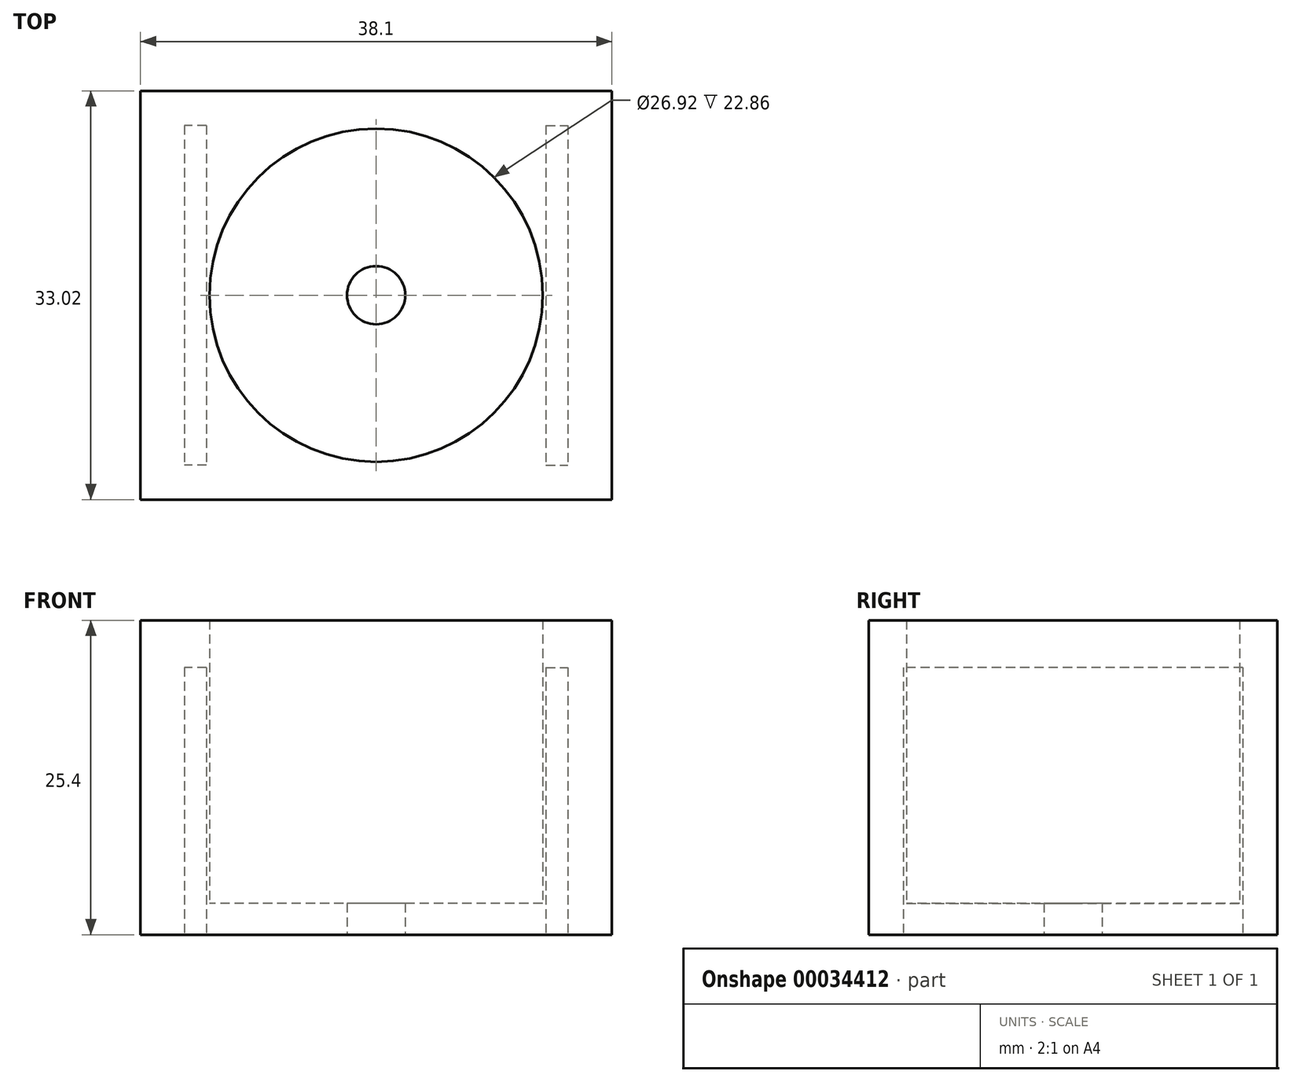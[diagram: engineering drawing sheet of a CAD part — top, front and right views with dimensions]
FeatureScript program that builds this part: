
annotation { "Feature Type Name" : "Feature", "Feature Type Description" : "" }
export const myFeature = defineFeature(function(context is Context, id is Id, definition is map)
    precondition{}
    {
        {
            var Q0;
            Q0=qCreatedBy(makeId("Top.planeOp"),FACE);
            var sketch = newSketch(context, id + "F0", { "sketchPlane" : qUnion([Q0])});
            skLineSegment(sketch, "E0.rect.bottom", {"start": v(19.05, 16.51) * mm, "end": v(-19.05, 16.51) * mm});
            skLineSegment(sketch, "E0.rect.top", {"start": v(19.05, -16.51) * mm, "end": v(-19.05, -16.51) * mm});
            skLineSegment(sketch, "E0.rect.left", {"start": v(19.05, 16.51) * mm, "end": v(19.05, -16.51) * mm});
            skLineSegment(sketch, "E0.rect.right", {"start": v(-19.05, 16.51) * mm, "end": v(-19.05, -16.51) * mm});
            skPoint(sketch, "E0.rect.middle", {"position": v(0, 0) * mm});
            skCircle(sketch, "E1", {"center": v(0, 0) * mm, "radius": 2.35 * mm});
            skSolve(sketch);
        }
        {
            var Q0;
            Q0=makeQuery(id+"F0.imprint","IMPRINT",FACE,{"disambiguationData":[TD([[makeQuery(id+"F0.imprint","IMPRINT",EDGE,{"derivedFrom":sQuery(id+"F0.wireOp",EDGE,"E0.rect.bottom")}),1.0]])]});
            extrude(context, id + "F1", {"entities" : qUnion([Q0]), "depth" : 2.54 * mm});
        }
        {
            var Q0;
            Q0=makeQuery(id+"F1.opExtrude","CAP_FACE",FACE,{"disambiguationData":[OSD([sQuery(id+"F0.wireOp",EDGE,"E0.rect.bottom"),sQuery(id+"F0.wireOp",EDGE,"E0.rect.top"),sQuery(id+"F0.wireOp",EDGE,"E0.rect.left"),sQuery(id+"F0.wireOp",EDGE,"E0.rect.right"),sQuery(id+"F0.wireOp",EDGE,"E1")])],"isStart":false});
            var sketch = newSketch(context, id + "F2", { "sketchPlane" : qUnion([Q0])});
            skCircle(sketch, "E2", {"center": v(0, 0) * mm, "radius": 13.46 * mm});
            skSolve(sketch);
        }
        {
            var Q0;
            Q0=makeQuery(id+"F2.imprint","IMPRINT",FACE,{"disambiguationData":[TD([[makeQuery(id+"F2.imprint","IMPRINT",EDGE,{"derivedFrom":sQuery(id+"F2.wireOp",EDGE,"E2")}),-1.0]])]});
            extrude(context, id + "F3", {"entities" : qUnion([Q0]), "operationType" : NewBodyOperationType.ADD, "depth" : 22.86 * mm});
        }
        {
            var Q0;
            Q0=makeQuery(id+"F1.opExtrude","CAP_FACE",FACE,{"disambiguationData":[OSD([sQuery(id+"F0.wireOp",EDGE,"E0.rect.bottom"),sQuery(id+"F0.wireOp",EDGE,"E0.rect.top"),sQuery(id+"F0.wireOp",EDGE,"E0.rect.left"),sQuery(id+"F0.wireOp",EDGE,"E0.rect.right"),sQuery(id+"F0.wireOp",EDGE,"E1")])],"isStart":true});
            var sketch = newSketch(context, id + "F4", { "sketchPlane" : qUnion([Q0])});
            skLineSegment(sketch, "E3", {"start": v(0, -16.51) * mm, "end": v(0, 16.51) * mm, "construction": true});
            skLineSegment(sketch, "E4", {"start": v(19.05, 0) * mm, "end": v(-19.05, 0) * mm, "construction": true});
            skLineSegment(sketch, "E5.rect.bottom", {"start": v(-13.72, -13.72) * mm, "end": v(-15.5, -13.72) * mm});
            skLineSegment(sketch, "E5.rect.top", {"start": v(-13.72, 13.72) * mm, "end": v(-15.5, 13.72) * mm});
            skLineSegment(sketch, "E5.rect.left", {"start": v(-13.72, -13.72) * mm, "end": v(-13.72, 13.72) * mm});
            skLineSegment(sketch, "E5.rect.right", {"start": v(-15.5, -13.72) * mm, "end": v(-15.5, 13.72) * mm});
            skPoint(sketch, "E5.rect.middle", {"position": v(-14.6, 0) * mm});
            skLineSegment(sketch, "E6.MirrorCS", {"start": v(13.72, -13.72) * mm, "end": v(13.72, 13.72) * mm});
            skLineSegment(sketch, "E7.MirrorCS", {"start": v(15.5, -13.72) * mm, "end": v(15.5, 13.72) * mm});
            skLineSegment(sketch, "E8.MirrorCS", {"start": v(13.72, -13.72) * mm, "end": v(15.5, -13.72) * mm});
            skLineSegment(sketch, "E9.MirrorCS", {"start": v(13.72, 13.72) * mm, "end": v(15.5, 13.72) * mm});
            skSolve(sketch);
        }
        {
            var Q0;
            Q0=makeQuery(id+"F4.imprint","IMPRINT",FACE,{"disambiguationData":[TD([[makeQuery(id+"F4.imprint","IMPRINT",EDGE,{"derivedFrom":sQuery(id+"F4.wireOp",EDGE,"E6.MirrorCS")}),-1.0]])]});
            var Q1;
            Q1=makeQuery(id+"F4.imprint","IMPRINT",FACE,{"disambiguationData":[TD([[makeQuery(id+"F4.imprint","IMPRINT",EDGE,{"derivedFrom":sQuery(id+"F4.wireOp",EDGE,"E5.rect.bottom")}),-1.0]])]});
            extrude(context, id + "F5", {"entities" : qUnion([Q0, Q1]), "operationType" : NewBodyOperationType.REMOVE, "oppositeDirection" : true, "depth" : 21.59 * mm});
        }
    });
